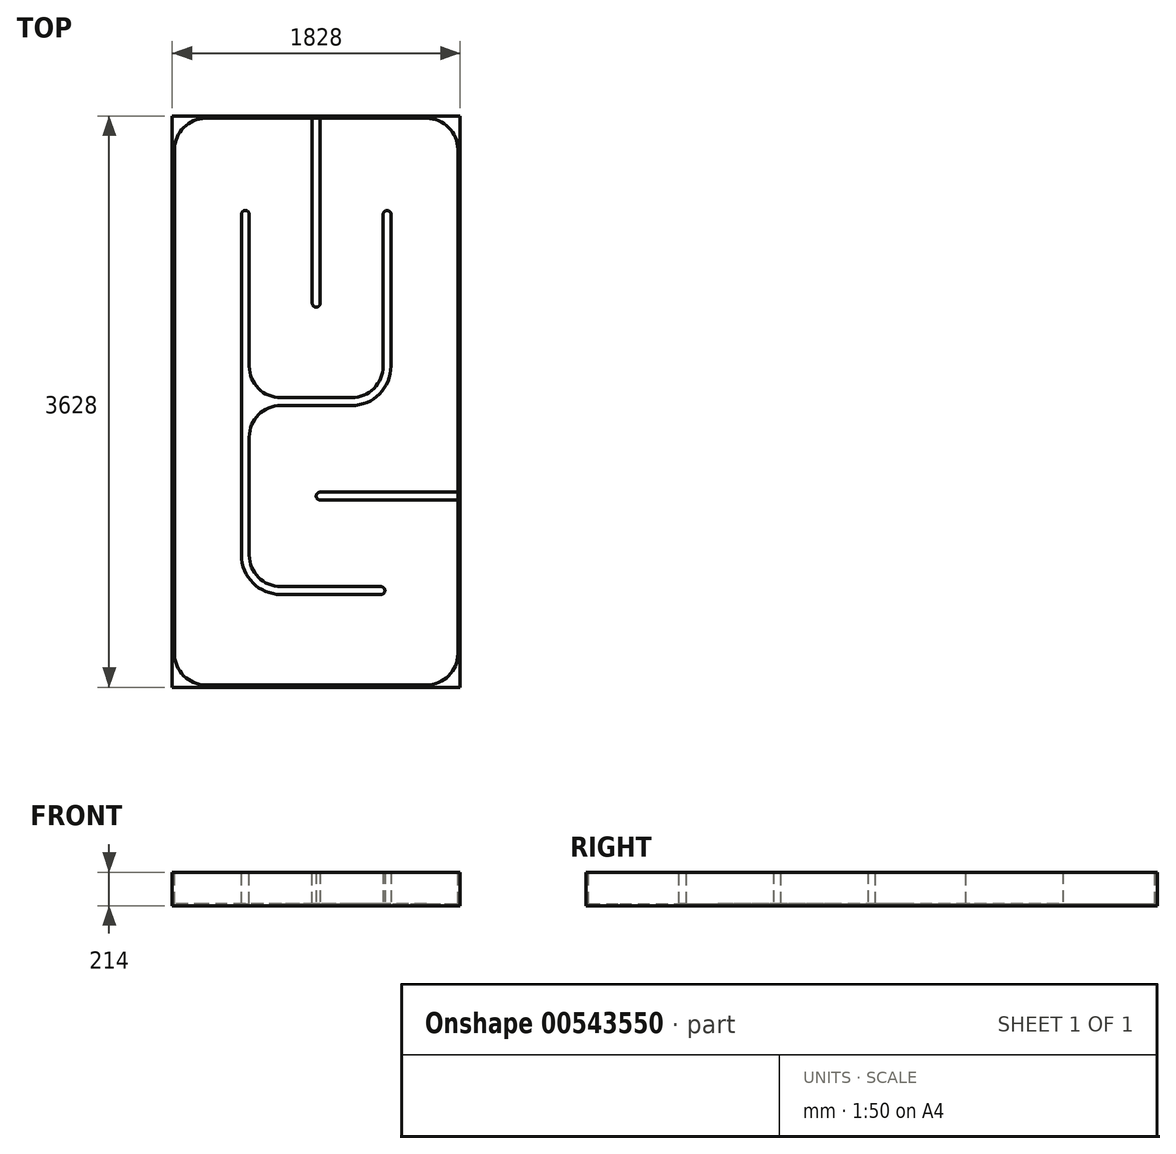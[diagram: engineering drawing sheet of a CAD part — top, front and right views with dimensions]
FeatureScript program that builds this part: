
annotation { "Feature Type Name" : "Feature", "Feature Type Description" : "" }
export const myFeature = defineFeature(function(context is Context, id is Id, definition is map)
    precondition{}
    {
        {
            assignVariable(context, id + "F0", {"name" : "atumi", "anyValue" : 14});
        }
        {
            assignVariable(context, id + "F1", {"name" : "tatehaba", "anyValue" : 600});
        }
        {
            assignVariable(context, id + "F2", {"name" : "R", "anyValue" : 200});
        }
        {
            assignVariable(context, id + "F3", {"name" : "takasa", "anyValue" : 200});
        }
        {
            assignVariable(context, id + "F4", {"name" : "haba", "anyValue" : 50});
        }
        {
            assignVariable(context, id + "F5", {"name" : "offset", "anyValue" : 25});
        }
        {
            var Q0;
            Q0=qCreatedBy(makeId("Top.planeOp"),FACE);
            var sketch = newSketch(context, id + "F6", { "sketchPlane" : qUnion([Q0])});
            skLineSegment(sketch, "E0.bottom", {"start": v(914, -1814) * mm, "end": v(-914, -1814) * mm});
            skLineSegment(sketch, "E0.top", {"start": v(914, 1814) * mm, "end": v(-914, 1814) * mm});
            skLineSegment(sketch, "E0.left", {"start": v(914, -1814) * mm, "end": v(914, 1814) * mm});
            skLineSegment(sketch, "E0.right", {"start": v(-914, -1814) * mm, "end": v(-914, 1814) * mm});
            skPoint(sketch, "E0.middle", {"position": v(0, 0) * mm});
            skSolve(sketch);
        }
        {
            var Q0;
            Q0 = qSketchRegion(id + "F6", true);
            extrude(context, id + "F7", {"entities" : qUnion([Q0]), "oppositeDirection" : true, "depth" : (getVariable(context, 'atumi')) * mm, "offsetDistance" : 25 * mm, "hasSecondDirection" : true, "secondDirectionOppositeDirection" : false, "secondDirectionDepth" : (getVariable(context, 'takasa')) * mm});
        }
        {
            var Q0;
            Q0=makeQuery(id+"F7.opExtrude","CAP_FACE",FACE,{"disambiguationData":[OSD([sQuery(id+"F6.wireOp",EDGE,"E0.bottom"),sQuery(id+"F6.wireOp",EDGE,"E0.top"),sQuery(id+"F6.wireOp",EDGE,"E0.left"),sQuery(id+"F6.wireOp",EDGE,"E0.right")])],"isStart":true});
            shell(context, id + "F8", {"entities" : qUnion([Q0]), "thickness" : (getVariable(context, 'atumi')) * mm});
        }
        {
            var Q0;
            Q0=makeQuery(id+"F6.imprint","IMPRINT",FACE,{"disambiguationData":[TD([[makeQuery(id+"F6.imprint","IMPRINT",EDGE,{"derivedFrom":sQuery(id+"F6.wireOp",EDGE,"E0.bottom")}),-1.0]])]});
            var sketch = newSketch(context, id + "F9", { "sketchPlane" : qUnion([Q0])});
            skLineSegment(sketch, "E1", {"start": v(-450, 1200) * mm, "end": v(-450, -1200) * mm});
            skLineSegment(sketch, "E2", {"start": v(0, 1800) * mm, "end": v(0, 600) * mm});
            skLineSegment(sketch, "E3", {"start": v(450, 0) * mm, "end": v(-450, 0) * mm});
            skLineSegment(sketch, "E4.MirrorCS", {"start": v(450, 1200) * mm, "end": v(450, 0) * mm});
            skLineSegment(sketch, "E5", {"start": v(0, -600) * mm, "end": v(900, -600) * mm});
            skLineSegment(sketch, "E6.MirrorCS", {"start": v(450, -1200) * mm, "end": v(-450, -1200) * mm});
            skSolve(sketch);
        }
        {
            var Q0;
            Q0=makeQuery(id+"F7.opExtrude","SWEPT_FACE",FACE,{"disambiguationData":[OSD([sQuery(id+"F6.wireOp",EDGE,"E0.top")])]});
            cPlane(context, id + "F10", {"entities" : qUnion([Q0]), "cplaneType" : CPlaneType.OFFSET, "offset" : (getVariable(context, 'tatehaba')) * mm, "oppositeDirection" : true, "width" : 150 * mm, "height" : 150 * mm});
        }
        {
            var Q0;
            Q0=qCreatedBy(makeId("Front.planeOp"),FACE);
            var Q1;
            Q1=sQuery(id+"F9.wireOp",VERTEX,"E2.end");
            cPlane(context, id + "F11", {"entities" : qUnion([Q0, Q1]), "cplaneType" : CPlaneType.PLANE_POINT, "offset" : 25 * mm, "width" : 150 * mm, "height" : 150 * mm});
        }
        {
            var Q0;
            Q0=qCreatedBy(id+"F11.planeOp",FACE);
            var sketch = newSketch(context, id + "F12", { "sketchPlane" : qUnion([Q0])});
            skLineSegment(sketch, "E7.bottom", {"start": v(25, 0) * mm, "end": v(-25, 0) * mm});
            skLineSegment(sketch, "E7.top", {"start": v(25, 200) * mm, "end": v(-25, 200) * mm});
            skLineSegment(sketch, "E7.left", {"start": v(25, 0) * mm, "end": v(25, 200) * mm});
            skLineSegment(sketch, "E7.right", {"start": v(-25, 0) * mm, "end": v(-25, 200) * mm});
            skPoint(sketch, "E8.0", {"position": v(0, 0) * mm});
            skSolve(sketch);
        }
        {
            var Q0;
            Q0=qCreatedBy(id+"F10.planeOp",FACE);
            var sketch = newSketch(context, id + "F13", { "sketchPlane" : qUnion([Q0])});
            skLineSegment(sketch, "E9.bottom", {"start": v(475, 0) * mm, "end": v(425, 0) * mm});
            skLineSegment(sketch, "E9.top", {"start": v(475, 200) * mm, "end": v(425, 200) * mm});
            skLineSegment(sketch, "E9.left", {"start": v(475, 0) * mm, "end": v(475, 200) * mm});
            skLineSegment(sketch, "E9.right", {"start": v(425, 0) * mm, "end": v(425, 200) * mm});
            skPoint(sketch, "E10.0", {"position": v(450, 0) * mm});
            skLineSegment(sketch, "E11.bottom", {"start": v(-425, 0) * mm, "end": v(-475, 0) * mm});
            skLineSegment(sketch, "E11.top", {"start": v(-425, 200) * mm, "end": v(-475, 200) * mm});
            skLineSegment(sketch, "E11.left", {"start": v(-425, 0) * mm, "end": v(-425, 200) * mm});
            skLineSegment(sketch, "E11.right", {"start": v(-475, 0) * mm, "end": v(-475, 200) * mm});
            skPoint(sketch, "E12.0", {"position": v(-450, 0) * mm});
            skSolve(sketch);
        }
        {
            var Q0;
            Q0=qCreatedBy(makeId("Right.planeOp"),FACE);
            var sketch = newSketch(context, id + "F14", { "sketchPlane" : qUnion([Q0])});
            skLineSegment(sketch, "E13.bottom", {"start": v(-625, 0) * mm, "end": v(-575, 0) * mm});
            skLineSegment(sketch, "E13.top", {"start": v(-625, 200) * mm, "end": v(-575, 200) * mm});
            skLineSegment(sketch, "E13.left", {"start": v(-625, 0) * mm, "end": v(-625, 200) * mm});
            skLineSegment(sketch, "E13.right", {"start": v(-575, 0) * mm, "end": v(-575, 200) * mm});
            skPoint(sketch, "E14.0", {"position": v(-600, 0) * mm});
            skSolve(sketch);
        }
        {
            var Q0;
            Q0=makeQuery(id+"F14.imprint","IMPRINT",FACE,{"disambiguationData":[TD([[makeQuery(id+"F14.imprint","IMPRINT",EDGE,{"derivedFrom":sQuery(id+"F14.wireOp",EDGE,"E13.bottom")}),1.0]])]});
            var Q1;
            Q1=sQuery(id+"F9.wireOp",EDGE,"E5");
            sweep(context, id + "F15", {"profiles" : qUnion([Q0]), "path" : qUnion([Q1])});
        }
        {
            var Q0;
            Q0=makeQuery(id+"F13.imprint","IMPRINT",FACE,{"disambiguationData":[TD([[makeQuery(id+"F13.imprint","IMPRINT",EDGE,{"derivedFrom":sQuery(id+"F13.wireOp",EDGE,"E9.bottom")}),-1.0]])]});
            var Q1;
            Q1=sQuery(id+"F9.wireOp",EDGE,"E1");
            var Q2;
            Q2=sQuery(id+"F9.wireOp",EDGE,"E6.MirrorCS");
            sweep(context, id + "F16", {"profiles" : qUnion([Q0]), "path" : qUnion([Q1, Q2])});
        }
        {
            var Q0;
            Q0=makeQuery(id+"F12.imprint","IMPRINT",FACE,{"disambiguationData":[TD([[makeQuery(id+"F12.imprint","IMPRINT",EDGE,{"derivedFrom":sQuery(id+"F12.wireOp",EDGE,"E7.bottom")}),-1.0]])]});
            var Q1;
            Q1=sQuery(id+"F9.wireOp",EDGE,"E2");
            sweep(context, id + "F17", {"profiles" : qUnion([Q0]), "path" : qUnion([Q1])});
        }
        {
            var Q0;
            Q0=makeQuery(id+"F13.imprint","IMPRINT",FACE,{"disambiguationData":[TD([[makeQuery(id+"F13.imprint","IMPRINT",EDGE,{"derivedFrom":sQuery(id+"F13.wireOp",EDGE,"E11.bottom")}),-1.0]])]});
            var Q1;
            Q1=sQuery(id+"F9.wireOp",EDGE,"E4.MirrorCS");
            var Q2;
            Q2=sQuery(id+"F9.wireOp",EDGE,"E3");
            sweep(context, id + "F18", {"profiles" : qUnion([Q0]), "path" : qUnion([Q1, Q2])});
        }
        {
            var Q0;
            Q0=makeQuery(id+"F16.opSweep","SWEPT_BODY",BODY,{"disambiguationData":[OSD([sQuery(id+"F9.wireOp",EDGE,"E6.MirrorCS"),sQuery(id+"F13.wireOp",EDGE,"E9.bottom"),sQuery(id+"F13.wireOp",EDGE,"E9.top"),sQuery(id+"F13.wireOp",EDGE,"E9.left"),sQuery(id+"F13.wireOp",EDGE,"E9.right")])]});
            var Q1;
            Q1=makeQuery(id+"F18.opSweep","SWEPT_BODY",BODY,{"disambiguationData":[OSD([sQuery(id+"F9.wireOp",EDGE,"E3"),sQuery(id+"F13.wireOp",EDGE,"E11.bottom"),sQuery(id+"F13.wireOp",EDGE,"E11.top"),sQuery(id+"F13.wireOp",EDGE,"E11.left"),sQuery(id+"F13.wireOp",EDGE,"E11.right")])]});
            booleanBodies(context, id + "F19", {"operationType" : BooleanOperationType.UNION, "tools" : qUnion([Q0, Q1])});
        }
        {
            var Q0;
            Q0=makeQuery(id+"F19.opBoolean","INTERSECT",EDGE,{"derivedFrom":[makeQuery(id+"F16.opSweep","SWEPT_FACE",FACE,{"disambiguationData":[OSD([sQuery(id+"F9.wireOp",EDGE,"E1"),sQuery(id+"F13.wireOp",EDGE,"E9.right")])]}),makeQuery(id+"F18.opSweep","SWEPT_FACE",FACE,{"disambiguationData":[OSD([sQuery(id+"F9.wireOp",EDGE,"E3"),sQuery(id+"F13.wireOp",EDGE,"E11.right")])]})]});
            var Q1;
            Q1=makeQuery(id+"F16.opSweep","MID_CAP_EDGE",EDGE,{"disambiguationData":[OSD([sQuery(id+"F9.wireOp",VERTEX,"E6.MirrorCS.end"),sQuery(id+"F13.wireOp",EDGE,"E9.right")])],"capPos":1.0});
            var Q2;
            Q2=makeQuery(id+"F18.opSweep","MID_CAP_EDGE",EDGE,{"disambiguationData":[OSD([sQuery(id+"F9.wireOp",VERTEX,"E3.start"),sQuery(id+"F13.wireOp",EDGE,"E11.left")])],"capPos":1.0});
            var Q3;
            Q3=makeQuery(id+"F19.opBoolean","INTERSECT",EDGE,{"derivedFrom":[makeQuery(id+"F16.opSweep","SWEPT_FACE",FACE,{"disambiguationData":[OSD([sQuery(id+"F9.wireOp",EDGE,"E1"),sQuery(id+"F13.wireOp",EDGE,"E9.right")])]}),makeQuery(id+"F18.opSweep","SWEPT_FACE",FACE,{"disambiguationData":[OSD([sQuery(id+"F9.wireOp",EDGE,"E3"),sQuery(id+"F13.wireOp",EDGE,"E11.left")])]})]});
            var Q4;
            Q4=makeQuery(id+"F17.opSweep","CAP_EDGE",EDGE,{"disambiguationData":[OSD([sQuery(id+"F9.wireOp",VERTEX,"E2.start"),sQuery(id+"F12.wireOp",EDGE,"E7.left")])],"isStart":false});
            var Q5;
            Q5=makeQuery(id+"F8.opShell","OFFSET_EDGE",EDGE,{"disambiguationData":[OSD([sQuery(id+"F6.wireOp",EDGE,"E0.top"),sQuery(id+"F6.wireOp",EDGE,"E0.left")])]});
            var Q6;
            Q6=makeQuery(id+"F17.opSweep","CAP_EDGE",EDGE,{"disambiguationData":[OSD([sQuery(id+"F9.wireOp",VERTEX,"E2.start"),sQuery(id+"F12.wireOp",EDGE,"E7.right")])],"isStart":false});
            var Q7;
            Q7=makeQuery(id+"F8.opShell","OFFSET_EDGE",EDGE,{"disambiguationData":[OSD([sQuery(id+"F6.wireOp",EDGE,"E0.top"),sQuery(id+"F6.wireOp",EDGE,"E0.right")])]});
            var Q8;
            Q8=makeQuery(id+"F8.opShell","OFFSET_EDGE",EDGE,{"disambiguationData":[OSD([sQuery(id+"F6.wireOp",EDGE,"E0.bottom"),sQuery(id+"F6.wireOp",EDGE,"E0.right")])]});
            var Q9;
            Q9=makeQuery(id+"F15.opSweep","CAP_EDGE",EDGE,{"disambiguationData":[OSD([sQuery(id+"F9.wireOp",VERTEX,"E5.end"),sQuery(id+"F14.wireOp",EDGE,"E13.right")])],"isStart":false});
            var Q10;
            Q10=makeQuery(id+"F15.opSweep","CAP_EDGE",EDGE,{"disambiguationData":[OSD([sQuery(id+"F9.wireOp",VERTEX,"E5.end"),sQuery(id+"F14.wireOp",EDGE,"E13.left")])],"isStart":false});
            var Q11;
            Q11=makeQuery(id+"F8.opShell","OFFSET_EDGE",EDGE,{"disambiguationData":[OSD([sQuery(id+"F6.wireOp",EDGE,"E0.bottom"),sQuery(id+"F6.wireOp",EDGE,"E0.left")])]});
            fillet(context, id + "F20", {"entities" : qUnion([Q0, Q1, Q2, Q3, Q4, Q5, Q6, Q7, Q8, Q9, Q10, Q11]), "radius" : (getVariable(context, 'R')) * mm, "tangentPropagation" : true, "allowEdgeOverflow" : false});
        }
        {
            var Q0;
            Q0=makeQuery(id+"F16.opSweep","CAP_EDGE",EDGE,{"disambiguationData":[OSD([sQuery(id+"F9.wireOp",VERTEX,"E6.MirrorCS.start"),sQuery(id+"F13.wireOp",EDGE,"E9.right")])],"isStart":false});
            var Q1;
            Q1=makeQuery(id+"F16.opSweep","CAP_EDGE",EDGE,{"disambiguationData":[OSD([sQuery(id+"F9.wireOp",VERTEX,"E6.MirrorCS.start"),sQuery(id+"F13.wireOp",EDGE,"E9.left")])],"isStart":false});
            var Q2;
            Q2=makeQuery(id+"F18.opSweep","CAP_EDGE",EDGE,{"disambiguationData":[OSD([sQuery(id+"F9.wireOp",VERTEX,"E4.MirrorCS.start"),sQuery(id+"F13.wireOp",EDGE,"E11.left")])],"isStart":true});
            var Q3;
            Q3=makeQuery(id+"F18.opSweep","CAP_EDGE",EDGE,{"disambiguationData":[OSD([sQuery(id+"F9.wireOp",VERTEX,"E4.MirrorCS.start"),sQuery(id+"F13.wireOp",EDGE,"E11.right")])],"isStart":true});
            var Q4;
            Q4=makeQuery(id+"F17.opSweep","CAP_EDGE",EDGE,{"disambiguationData":[OSD([sQuery(id+"F9.wireOp",VERTEX,"E2.end"),sQuery(id+"F12.wireOp",EDGE,"E7.right")])],"isStart":true});
            var Q5;
            Q5=makeQuery(id+"F17.opSweep","CAP_EDGE",EDGE,{"disambiguationData":[OSD([sQuery(id+"F9.wireOp",VERTEX,"E2.end"),sQuery(id+"F12.wireOp",EDGE,"E7.left")])],"isStart":true});
            var Q6;
            Q6=makeQuery(id+"F16.opSweep","CAP_EDGE",EDGE,{"disambiguationData":[OSD([sQuery(id+"F9.wireOp",VERTEX,"E1.start"),sQuery(id+"F13.wireOp",EDGE,"E9.left")])],"isStart":true});
            var Q7;
            Q7=makeQuery(id+"F16.opSweep","CAP_EDGE",EDGE,{"disambiguationData":[OSD([sQuery(id+"F9.wireOp",VERTEX,"E1.start"),sQuery(id+"F13.wireOp",EDGE,"E9.right")])],"isStart":true});
            var Q8;
            Q8=makeQuery(id+"F15.opSweep","CAP_EDGE",EDGE,{"disambiguationData":[OSD([sQuery(id+"F9.wireOp",VERTEX,"E5.start"),sQuery(id+"F14.wireOp",EDGE,"E13.right")])],"isStart":true});
            var Q9;
            Q9=makeQuery(id+"F15.opSweep","CAP_EDGE",EDGE,{"disambiguationData":[OSD([sQuery(id+"F9.wireOp",VERTEX,"E5.start"),sQuery(id+"F14.wireOp",EDGE,"E13.left")])],"isStart":true});
            fillet(context, id + "F21", {"entities" : qUnion([Q0, Q1, Q2, Q3, Q4, Q5, Q6, Q7, Q8, Q9]), "radius" : (getVariable(context, 'offset')) * mm, "tangentPropagation" : true, "allowEdgeOverflow" : false});
        }
        {
            var Q0;
            Q0=makeQuery(id+"F18.opSweep","MID_CAP_EDGE",EDGE,{"disambiguationData":[OSD([sQuery(id+"F9.wireOp",VERTEX,"E3.start"),sQuery(id+"F13.wireOp",EDGE,"E11.right")])],"capPos":1.0});
            var Q1;
            Q1=makeQuery(id+"F16.opSweep","MID_CAP_EDGE",EDGE,{"disambiguationData":[OSD([sQuery(id+"F9.wireOp",VERTEX,"E6.MirrorCS.end"),sQuery(id+"F13.wireOp",EDGE,"E9.left")])],"capPos":1.0});
            fillet(context, id + "F22", {"entities" : qUnion([Q0, Q1]), "radius" : (getVariable(context, 'R') + getVariable(context, 'haba')) * mm, "tangentPropagation" : true, "allowEdgeOverflow" : false});
        }
    });
